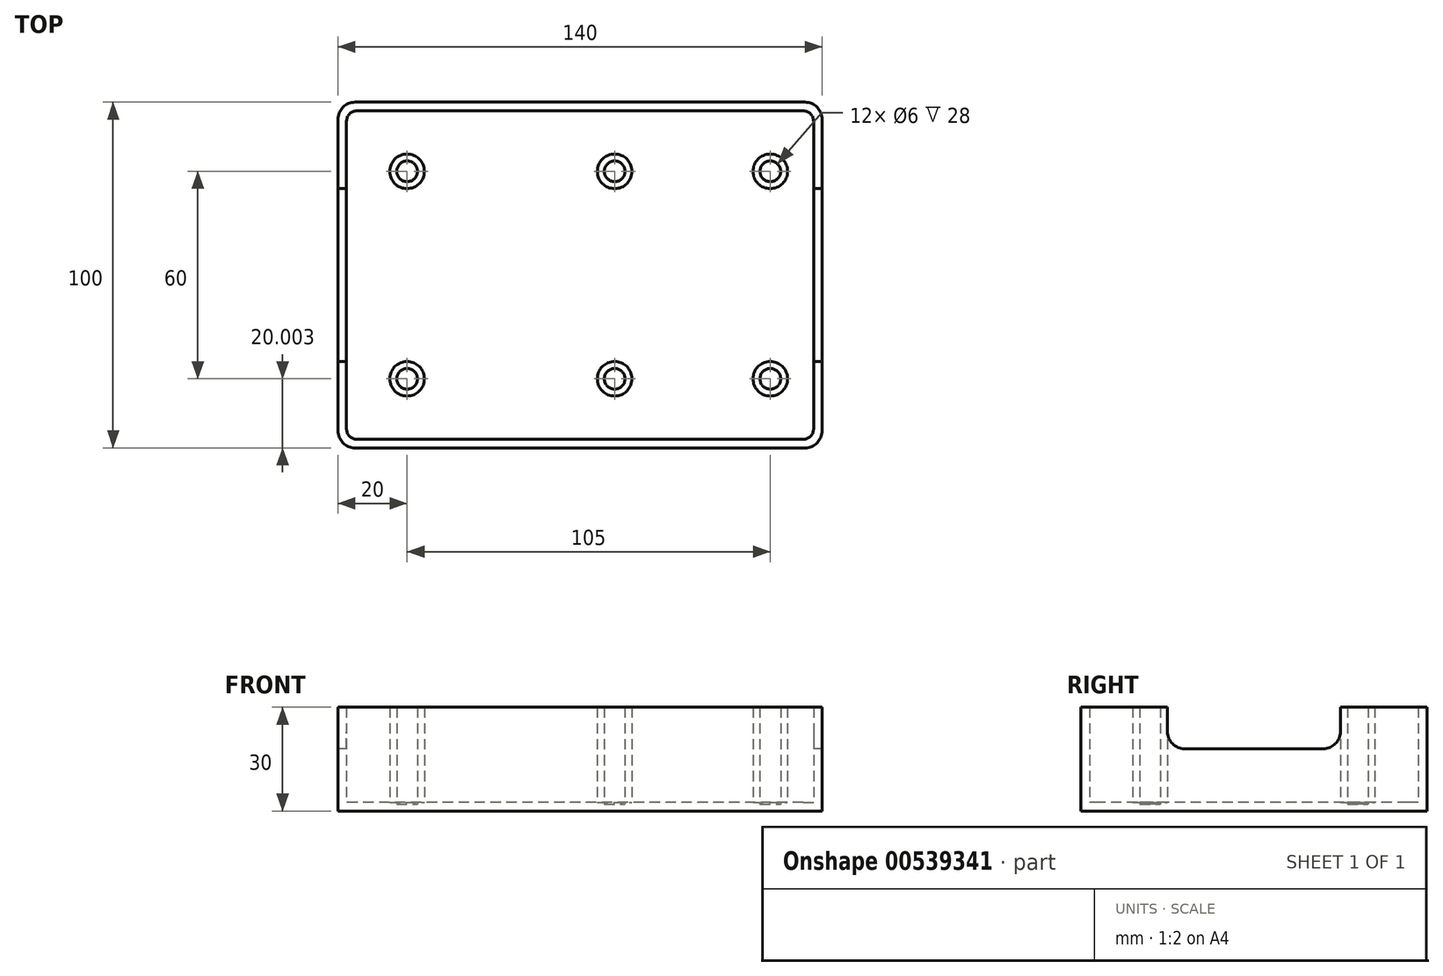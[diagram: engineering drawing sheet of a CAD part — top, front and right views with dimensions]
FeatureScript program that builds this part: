
annotation { "Feature Type Name" : "Feature", "Feature Type Description" : "" }
export const myFeature = defineFeature(function(context is Context, id is Id, definition is map)
    precondition{}
    {
        {
            var Q0;
            Q0=qCreatedBy(makeId("Top.planeOp"),FACE);
            var sketch = newSketch(context, id + "F0", { "sketchPlane" : qUnion([Q0])});
            skLineSegment(sketch, "E0.bottom", {"start": v(-20, -50) * mm, "end": v(120, -50) * mm});
            skLineSegment(sketch, "E0.top", {"start": v(-20, 50) * mm, "end": v(120, 50) * mm});
            skLineSegment(sketch, "E0.left", {"start": v(-20, -50) * mm, "end": v(-20, 50) * mm});
            skLineSegment(sketch, "E0.right", {"start": v(120, -50) * mm, "end": v(120, 50) * mm});
            skSolve(sketch);
        }
        {
            var Q0;
            Q0=makeQuery(id+"F0.imprint","IMPRINT",FACE,{"disambiguationData":[TD([[makeQuery(id+"F0.imprint","IMPRINT",EDGE,{"derivedFrom":sQuery(id+"F0.wireOp",EDGE,"E0.bottom")}),1.0]])]});
            extrude(context, id + "F1", {"entities" : qUnion([Q0]), "depth" : 30 * mm, "offsetDistance" : 25 * mm});
        }
        {
            var Q0;
            Q0=makeQuery(id+"F1.opExtrude","CAP_FACE",FACE,{"disambiguationData":[OSD([sQuery(id+"F0.wireOp",EDGE,"E0.bottom"),sQuery(id+"F0.wireOp",EDGE,"E0.top"),sQuery(id+"F0.wireOp",EDGE,"E0.left"),sQuery(id+"F0.wireOp",EDGE,"E0.right")])],"isStart":false});
            shell(context, id + "F2", {"entities" : qUnion([Q0]), "thickness" : 2.5 * mm});
        }
        {
            var Q0;
            Q0=makeQuery(id+"F1.opExtrude","SWEPT_FACE",FACE,{"disambiguationData":[OSD([sQuery(id+"F0.wireOp",EDGE,"E0.right")])]});
            var sketch = newSketch(context, id + "F3", { "sketchPlane" : qUnion([Q0])});
            skLineSegment(sketch, "E1.bottom", {"start": v(-25, 18) * mm, "end": v(25, 18) * mm});
            skLineSegment(sketch, "E1.top", {"start": v(-25, 45.31) * mm, "end": v(25, 45.31) * mm});
            skLineSegment(sketch, "E1.left", {"start": v(-25, 18) * mm, "end": v(-25, 45.31) * mm});
            skLineSegment(sketch, "E1.right", {"start": v(25, 18) * mm, "end": v(25, 45.31) * mm});
            skSolve(sketch);
        }
        {
            var Q0;
            {var subQ0=sQuery(id+"F3.wireOp",EDGE,"E1.bottom");Q0=makeQuery(id+"F3.imprint","IMPRINT",FACE,{"disambiguationData":[TD([[makeQuery(id+"F3.imprint","IMPRINT",EDGE,{"derivedFrom":subQ0}),1.0]])]});}
            extrude(context, id + "F4", {"entities" : qUnion([Q0]), "operationType" : NewBodyOperationType.REMOVE, "oppositeDirection" : true, "depth" : 205.5 * mm, "offsetDistance" : 25 * mm});
        }
        {
            var Q0;
            {var subQ0=sQuery(id+"F0.wireOp",EDGE,"E0.left");var subQ1=sQuery(id+"F3.wireOp",EDGE,"E1.bottom");var subQ2=sQuery(id+"F3.wireOp",EDGE,"E1.right");Q0=makeQuery(id+"F4.boolean.opBoolean","COPY",EDGE,{"disambiguationData":[TD([makeQuery(id+"F1.opExtrude","SWEPT_FACE",FACE,{"disambiguationData":[OSD([subQ0])]})])],"derivedFrom":makeQuery(id+"F4.opExtrude","SWEPT_EDGE",EDGE,{"disambiguationData":[OSD([subQ1,subQ2])]})});}
            var Q1;
            {var subQ0=sQuery(id+"F0.wireOp",EDGE,"E0.left");var subQ1=sQuery(id+"F3.wireOp",EDGE,"E1.bottom");var subQ2=sQuery(id+"F3.wireOp",EDGE,"E1.left");Q1=makeQuery(id+"F4.boolean.opBoolean","COPY",EDGE,{"disambiguationData":[TD([makeQuery(id+"F1.opExtrude","SWEPT_FACE",FACE,{"disambiguationData":[OSD([subQ0])]})])],"derivedFrom":makeQuery(id+"F4.opExtrude","SWEPT_EDGE",EDGE,{"disambiguationData":[OSD([subQ1,subQ2])]})});}
            var Q2;
            {var subQ0=sQuery(id+"F0.wireOp",EDGE,"E0.right");var subQ1=sQuery(id+"F3.wireOp",EDGE,"E1.bottom");var subQ2=sQuery(id+"F3.wireOp",EDGE,"E1.left");Q2=makeQuery(id+"F4.boolean.opBoolean","COPY",EDGE,{"disambiguationData":[TD([makeQuery(id+"F1.opExtrude","SWEPT_FACE",FACE,{"disambiguationData":[OSD([subQ0])]})])],"derivedFrom":makeQuery(id+"F4.opExtrude","SWEPT_EDGE",EDGE,{"disambiguationData":[OSD([subQ1,subQ2])]})});}
            var Q3;
            {var subQ0=sQuery(id+"F0.wireOp",EDGE,"E0.right");var subQ1=sQuery(id+"F3.wireOp",EDGE,"E1.bottom");var subQ2=sQuery(id+"F3.wireOp",EDGE,"E1.right");Q3=makeQuery(id+"F4.boolean.opBoolean","COPY",EDGE,{"disambiguationData":[TD([makeQuery(id+"F1.opExtrude","SWEPT_FACE",FACE,{"disambiguationData":[OSD([subQ0])]})])],"derivedFrom":makeQuery(id+"F4.opExtrude","SWEPT_EDGE",EDGE,{"disambiguationData":[OSD([subQ1,subQ2])]})});}
            fillet(context, id + "F5", {"entities" : qUnion([Q0, Q1, Q2, Q3]), "radius" : 5 * mm, "tangentPropagation" : true, "allowEdgeOverflow" : false});
        }
        {
            var Q0;
            Q0=makeQuery(id+"F1.opExtrude","SWEPT_EDGE",EDGE,{"disambiguationData":[OSD([sQuery(id+"F0.wireOp",EDGE,"E0.top"),sQuery(id+"F0.wireOp",EDGE,"E0.right")])]});
            var Q1;
            Q1=makeQuery(id+"F1.opExtrude","SWEPT_EDGE",EDGE,{"disambiguationData":[OSD([sQuery(id+"F0.wireOp",EDGE,"E0.top"),sQuery(id+"F0.wireOp",EDGE,"E0.left")])]});
            var Q2;
            Q2=makeQuery(id+"F1.opExtrude","SWEPT_EDGE",EDGE,{"disambiguationData":[OSD([sQuery(id+"F0.wireOp",EDGE,"E0.bottom"),sQuery(id+"F0.wireOp",EDGE,"E0.left")])]});
            var Q3;
            Q3=makeQuery(id+"F1.opExtrude","SWEPT_EDGE",EDGE,{"disambiguationData":[OSD([sQuery(id+"F0.wireOp",EDGE,"E0.bottom"),sQuery(id+"F0.wireOp",EDGE,"E0.right")])]});
            fillet(context, id + "F6", {"entities" : qUnion([Q0, Q1, Q2, Q3]), "radius" : 5 * mm, "tangentPropagation" : true, "allowEdgeOverflow" : false});
        }
        {
            var Q0;
            Q0=makeQuery(id+"F2.opShell","OFFSET_EDGE",EDGE,{"disambiguationData":[OSD([sQuery(id+"F0.wireOp",EDGE,"E0.bottom"),sQuery(id+"F0.wireOp",EDGE,"E0.left")])]});
            var Q1;
            Q1=makeQuery(id+"F2.opShell","OFFSET_EDGE",EDGE,{"disambiguationData":[OSD([sQuery(id+"F0.wireOp",EDGE,"E0.top"),sQuery(id+"F0.wireOp",EDGE,"E0.left")])]});
            var Q2;
            Q2=makeQuery(id+"F2.opShell","OFFSET_EDGE",EDGE,{"disambiguationData":[OSD([sQuery(id+"F0.wireOp",EDGE,"E0.top"),sQuery(id+"F0.wireOp",EDGE,"E0.right")])]});
            var Q3;
            Q3=makeQuery(id+"F2.opShell","OFFSET_EDGE",EDGE,{"disambiguationData":[OSD([sQuery(id+"F0.wireOp",EDGE,"E0.bottom"),sQuery(id+"F0.wireOp",EDGE,"E0.right")])]});
            fillet(context, id + "F7", {"entities" : qUnion([Q0, Q1, Q2, Q3]), "radius" : 3 * mm, "tangentPropagation" : true, "allowEdgeOverflow" : false});
        }
        {
            var Q0;
            Q0=makeQuery(id+"F2.opShell","OFFSET_FACE",FACE,{"disambiguationData":[OSD([sQuery(id+"F0.wireOp",EDGE,"E0.bottom"),sQuery(id+"F0.wireOp",EDGE,"E0.top"),sQuery(id+"F0.wireOp",EDGE,"E0.left"),sQuery(id+"F0.wireOp",EDGE,"E0.right")])]});
            var sketch = newSketch(context, id + "F8", { "sketchPlane" : qUnion([Q0])});
            skCircle(sketch, "E2", {"center": v(-5, -30) * mm, "radius": 5 * mm});
            skCircle(sketch, "E3", {"center": v(100, -30) * mm, "radius": 5 * mm});
            skCircle(sketch, "E4", {"center": v(100, 30) * mm, "radius": 5 * mm});
            skCircle(sketch, "E5", {"center": v(-5, 30) * mm, "radius": 5 * mm});
            skCircle(sketch, "E6", {"center": v(40, -30) * mm, "radius": 5 * mm});
            skCircle(sketch, "E7", {"center": v(40, 30) * mm, "radius": 5 * mm});
            skSolve(sketch);
        }
        {
            var Q0;
            Q0=makeQuery(id+"F8.imprint","IMPRINT",FACE,{"disambiguationData":[TD([[makeQuery(id+"F8.imprint","IMPRINT",EDGE,{"derivedFrom":sQuery(id+"F8.wireOp",EDGE,"E2")}),1.0]])]});
            var Q1;
            Q1=makeQuery(id+"F8.imprint","IMPRINT",FACE,{"disambiguationData":[TD([[makeQuery(id+"F8.imprint","IMPRINT",EDGE,{"derivedFrom":sQuery(id+"F8.wireOp",EDGE,"E6")}),1.0]])]});
            var Q2;
            Q2=makeQuery(id+"F8.imprint","IMPRINT",FACE,{"disambiguationData":[TD([[makeQuery(id+"F8.imprint","IMPRINT",EDGE,{"derivedFrom":sQuery(id+"F8.wireOp",EDGE,"E3")}),1.0]])]});
            var Q3;
            Q3=makeQuery(id+"F8.imprint","IMPRINT",FACE,{"disambiguationData":[TD([[makeQuery(id+"F8.imprint","IMPRINT",EDGE,{"derivedFrom":sQuery(id+"F8.wireOp",EDGE,"E4")}),1.0]])]});
            var Q4;
            Q4=makeQuery(id+"F8.imprint","IMPRINT",FACE,{"disambiguationData":[TD([[makeQuery(id+"F8.imprint","IMPRINT",EDGE,{"derivedFrom":sQuery(id+"F8.wireOp",EDGE,"E7")}),1.0]])]});
            var Q5;
            Q5=makeQuery(id+"F8.imprint","IMPRINT",FACE,{"disambiguationData":[TD([[makeQuery(id+"F8.imprint","IMPRINT",EDGE,{"derivedFrom":sQuery(id+"F8.wireOp",EDGE,"E5")}),1.0]])]});
            var Q6;
            {var subQ0=sQuery(id+"F0.wireOp",EDGE,"E0.bottom");var subQ1=sQuery(id+"F0.wireOp",EDGE,"E0.left");var subQ2=sQuery(id+"F0.wireOp",EDGE,"E0.right");Q6=makeQuery(id+"F4.boolean.opBoolean","SPLIT",FACE,{"disambiguationData":[TD([makeQuery(id+"F1.opExtrude","SWEPT_FACE",FACE,{"disambiguationData":[OSD([subQ0])]})])],"derivedFrom":makeQuery(id+"F1.opExtrude","CAP_FACE",FACE,{"disambiguationData":[OSD([subQ0,sQuery(id+"F0.wireOp",EDGE,"E0.top"),subQ1,subQ2])],"isStart":false})});}
            extrude(context, id + "F9", {"entities" : qUnion([Q0, Q1, Q2, Q3, Q4, Q5]), "operationType" : NewBodyOperationType.ADD, "endBound" : BoundingType.UP_TO_SURFACE, "depth" : 25 * mm, "endBoundEntityFace" : qUnion([Q6]), "offsetDistance" : 25 * mm});
        }
        {
            var Q0;
            Q0=makeQuery(id+"F9.opExtrude","CAP_FACE",FACE,{"disambiguationData":[OSD([sQuery(id+"F8.wireOp",EDGE,"E2")])],"isStart":false});
            var Q1;
            Q1=makeQuery(id+"F9.opExtrude","CAP_FACE",FACE,{"disambiguationData":[OSD([sQuery(id+"F8.wireOp",EDGE,"E6")])],"isStart":false});
            var Q2;
            Q2=makeQuery(id+"F9.opExtrude","CAP_FACE",FACE,{"disambiguationData":[OSD([sQuery(id+"F8.wireOp",EDGE,"E5")])],"isStart":false});
            var Q3;
            Q3=makeQuery(id+"F9.opExtrude","CAP_FACE",FACE,{"disambiguationData":[OSD([sQuery(id+"F8.wireOp",EDGE,"E7")])],"isStart":false});
            var Q4;
            Q4=makeQuery(id+"F9.opExtrude","CAP_FACE",FACE,{"disambiguationData":[OSD([sQuery(id+"F8.wireOp",EDGE,"E3")])],"isStart":false});
            var Q5;
            Q5=makeQuery(id+"F9.opExtrude","CAP_FACE",FACE,{"disambiguationData":[OSD([sQuery(id+"F8.wireOp",EDGE,"E4")])],"isStart":false});
            shell(context, id + "F10", {"entities" : qUnion([Q0, Q1, Q2, Q3, Q4, Q5]), "thickness" : 2 * mm});
        }
        {
            var Q0;
            Q0=makeQuery(id+"F1.opExtrude","SWEPT_BODY",BODY,{"disambiguationData":[OSD([sQuery(id+"F0.wireOp",EDGE,"E0.bottom"),sQuery(id+"F0.wireOp",EDGE,"E0.top"),sQuery(id+"F0.wireOp",EDGE,"E0.left"),sQuery(id+"F0.wireOp",EDGE,"E0.right")])]});
            var Q1;
            Q1=makeQuery(id+"F10.opShell","OFFSET_EDGE",EDGE,{"disambiguationData":[OSD([sQuery(id+"F8.wireOp",EDGE,"E5")])]});
            transform(context, id + "F11", {"entities" : qUnion([Q0]), "transformType" : TransformType.ROTATION, "transformAxis" : qUnion([Q1]), "angle" : 60 * degree, "makeCopy" : false});
        }
        {
            var Q0;
            Q0=makeQuery(id+"F1.opExtrude","SWEPT_BODY",BODY,{"disambiguationData":[OSD([sQuery(id+"F0.wireOp",EDGE,"E0.bottom"),sQuery(id+"F0.wireOp",EDGE,"E0.top"),sQuery(id+"F0.wireOp",EDGE,"E0.left"),sQuery(id+"F0.wireOp",EDGE,"E0.right")])]});
            var Q1;
            Q1=makeQuery(id+"F10.opShell","OFFSET_FACE",FACE,{"disambiguationData":[OSD([sQuery(id+"F8.wireOp",EDGE,"E4")])]});
            transform(context, id + "F12", {"entities" : qUnion([Q0]), "transformType" : TransformType.ROTATION, "transformAxis" : qUnion([Q1]), "angle" : 30 * degree, "makeCopy" : false});
        }
        {
            var Q0;
            Q0=makeQuery(id+"F1.opExtrude","SWEPT_BODY",BODY,{"disambiguationData":[OSD([sQuery(id+"F0.wireOp",EDGE,"E0.bottom"),sQuery(id+"F0.wireOp",EDGE,"E0.top"),sQuery(id+"F0.wireOp",EDGE,"E0.left"),sQuery(id+"F0.wireOp",EDGE,"E0.right")])]});
            var Q1;
            Q1=makeQuery(id+"F10.opShell","OFFSET_FACE",FACE,{"disambiguationData":[OSD([sQuery(id+"F8.wireOp",EDGE,"E4")])]});
            transform(context, id + "F13", {"entities" : qUnion([Q0]), "transformType" : TransformType.ROTATION, "transformAxis" : qUnion([Q1]), "angle" : 90 * degree, "makeCopy" : false});
        }
    });
